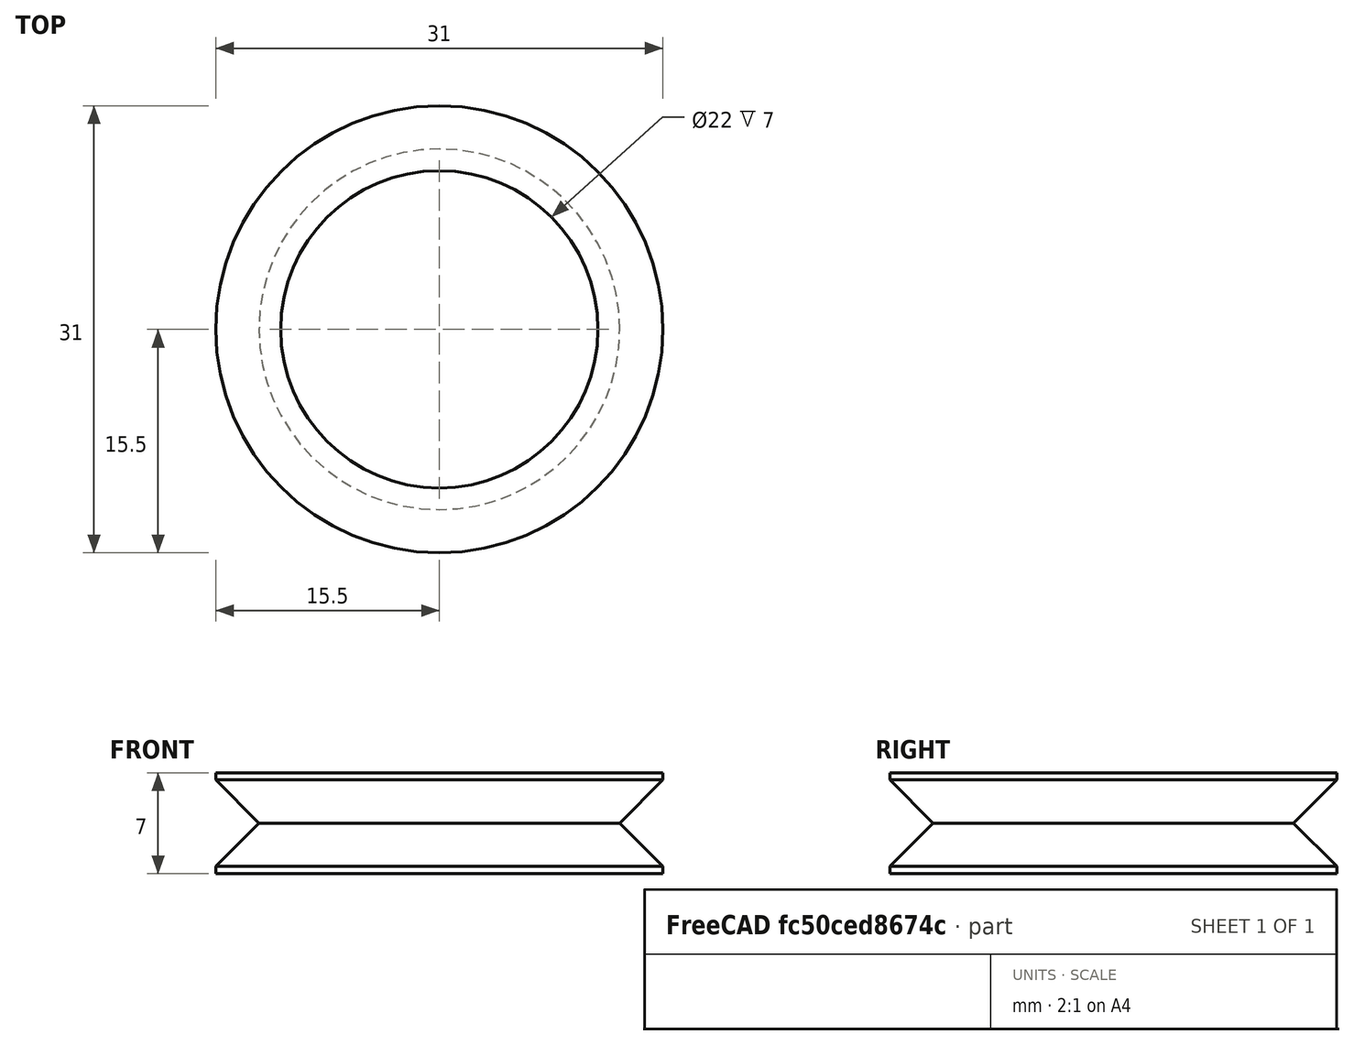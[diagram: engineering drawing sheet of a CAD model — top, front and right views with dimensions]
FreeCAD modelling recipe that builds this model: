
FCSTD DOCUMENT  (FreeCAD 0.20R27319 (Git))
Label: GroovedRingWithBearing
License: All rights reserved
LicenseURL: http://en.wikipedia.org/wiki/All_rights_reserved
objects: Sketcher::SketchObject×1, PartDesign::Revolution×1, PartDesign::Body×1, Spreadsheet::Sheet×1
note: 4 computed .brp shape members not serialized (recipe doc carries the construction recipe); baked Part::Feature solids carry a one-line shape summary decoded from their .brp

FEATURE [Sketcher::SketchObject] Sketch
  FullyConstrained = true
  MapMode = 5
  Placement = pos=(0,0,0) rot=(1,0,0;1.5708rad)
  Support = -> [XZ_Plane]
  expr: Constraints[13] = Spreadsheet.PulleyInnerDiameter / 2
  expr: Constraints[23] = Spreadsheet.PulleyOuterDiameter / 2
  expr: Constraints[5] = Spreadsheet.BearingThickness
  expr: Constraints[6] = Spreadsheet.BearingOuterDiameter / 2
  sketch-geometry (9):
    g0: LineSegment StartX=11 StartY=3.5 StartZ=0 EndX=15.5 EndY=3.5 EndZ=0
    g1: LineSegment StartX=11 StartY=3.5 StartZ=0 EndX=11 EndY=-3.5 EndZ=0
    g2: LineSegment StartX=11 StartY=-3.5 StartZ=0 EndX=15.5 EndY=-3.5 EndZ=0
    g3: LineSegment StartX=15.5 StartY=3.5 StartZ=0 EndX=15.5 EndY=3 EndZ=0
    g4: LineSegment StartX=15.5 StartY=-3 StartZ=0 EndX=15.5 EndY=-3.5 EndZ=0
    g5: GeomPoint X=12.5 Y=0 Z=0
    g6: LineSegment StartX=12.5 StartY=0 StartZ=0 EndX=15.5 EndY=3 EndZ=0
    g7: LineSegment StartX=12.5 StartY=0 StartZ=0 EndX=15.5 EndY=-3 EndZ=0
    g8: ArcOfCircle CenterX=15.5 CenterY=0 CenterZ=0 NormalX=0 NormalY=0 NormalZ=1 AngleXU=0 Radius=3 StartAngle=1.5708 EndAngle=4.71239
  constraints (24):
    c: Horizontal(g0)
    c: Coincident(g0,g1)
    c: Coincident(g1,g2)
    c: Horizontal(g2)
    c: Symmetric(g0,g1,g-1)
    c: DistanceY(g1,g1) = 7
    c: DistanceX(g-1,g0) = 11
    c: Vertical(g0,g2)
    c: Coincident(g3,g0)
    c: Coincident(g4,g2)
    c: Vertical(g3)
    c: Vertical(g4)
    c: PointOnObject(g5,g-1)
    c: DistanceX(g-1,g5) = 12.5
    c: Equal(g3,g4)
    c: Coincident(g6,g5)
    c: Coincident(g6,g3)
    c: Coincident(g7,g6)
    c: Coincident(g7,g4)
    c: Angle(g7,g6) = 1.5708
    c: Coincident(g8,g3)
    c: Coincident(g8,g4)
    c: PointOnObject(g6,g8)
    c: DistanceX(g-1,g0) = 15.5
FEATURE [PartDesign::Revolution] Revolution
  Angle = 360
  Axis = (0,-2e-16,1)
  Base = (0,0,0)
  Placement = pos=(0,0,0) rot=(1,0,0;1.5708rad)
  Profile = -> Sketch
  ReferenceAxis = -> Sketch [V_Axis]
  Reversed = true
FEATURE [PartDesign::Body] Body
  Group = -> [Sketch,Revolution]
  Origin = -> Origin
  Tip = -> Revolution
FEATURE [Spreadsheet::Sheet] Spreadsheet
  cells = A1=Pulley Outer Diameter; B1(PulleyOuterDiameter)==B2 + 6; A2=Pulley Inner Diameter; B2(PulleyInnerDiameter)=25; A3=Bearing Outer Diameter; B3(BearingOuterDiameter)=22; A4=Bearing Inner Diameter; B4(BearingInnerDiameter)=8; A5=Bearing Thickness; B5(BearingThickness)=7
